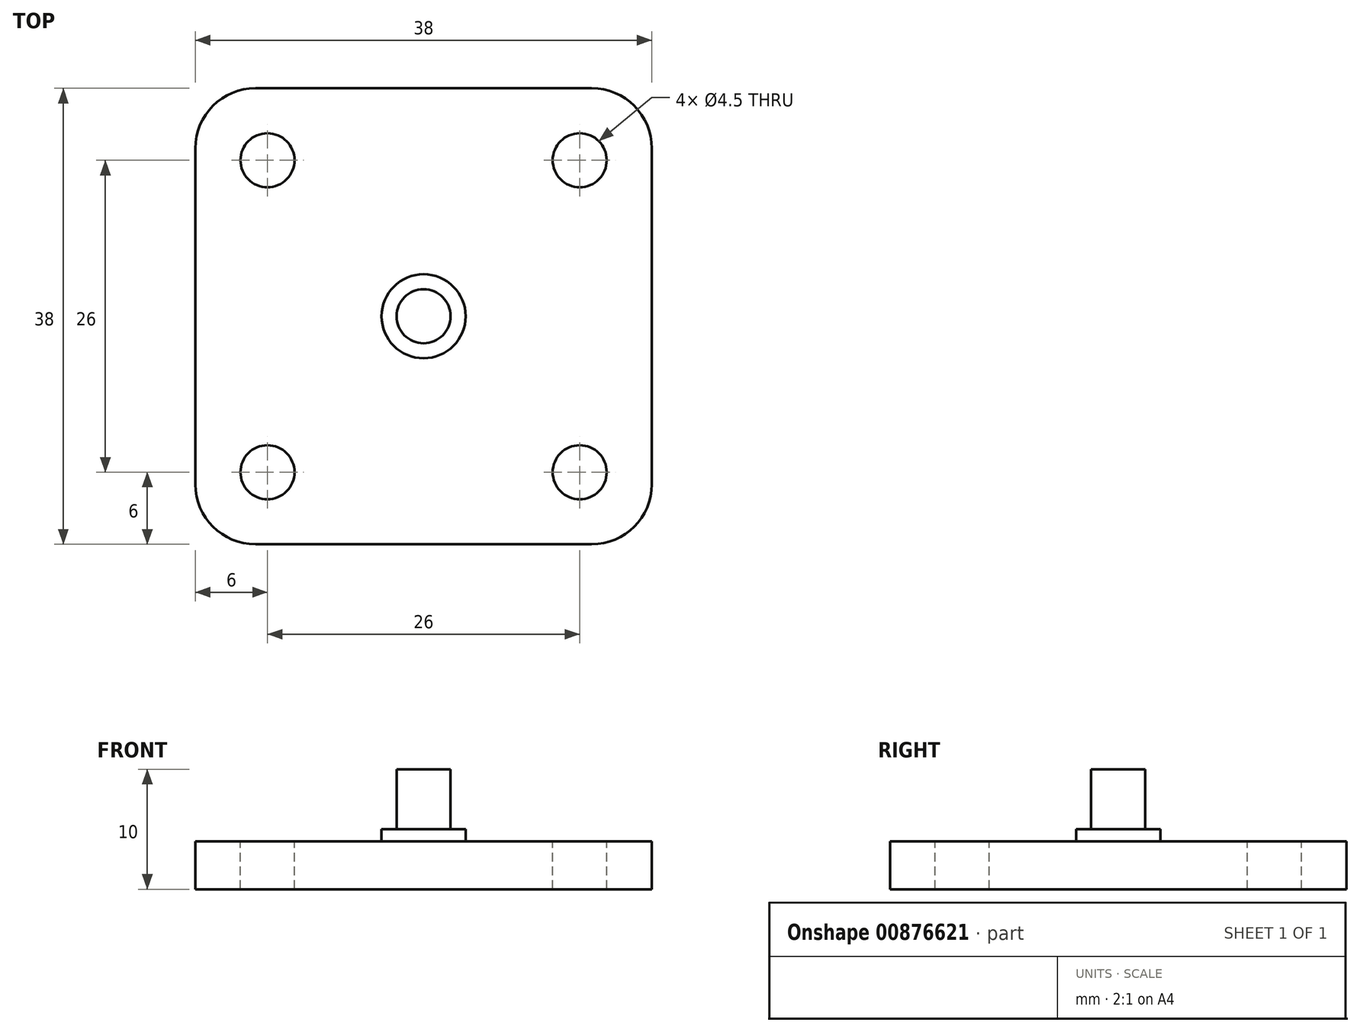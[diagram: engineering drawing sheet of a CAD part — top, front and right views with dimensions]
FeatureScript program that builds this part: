
annotation { "Feature Type Name" : "Feature", "Feature Type Description" : "" }
export const myFeature = defineFeature(function(context is Context, id is Id, definition is map)
    precondition{}
    {
        {
            var Q0;
            Q0=qCreatedBy(makeId("Top.planeOp"),FACE);
            var sketch = newSketch(context, id + "F0", { "sketchPlane" : qUnion([Q0])});
            skLineSegment(sketch, "E0.bottom", {"start": v(19, 19) * mm, "end": v(-19, 19) * mm});
            skLineSegment(sketch, "E0.top", {"start": v(19, -19) * mm, "end": v(-19, -19) * mm});
            skLineSegment(sketch, "E0.left", {"start": v(19, 19) * mm, "end": v(19, -19) * mm});
            skLineSegment(sketch, "E0.right", {"start": v(-19, 19) * mm, "end": v(-19, -19) * mm});
            skPoint(sketch, "E0.middle", {"position": v(0, 0) * mm});
            skLineSegment(sketch, "E1.0", {"start": v(19, 13) * mm, "end": v(-19, 13) * mm, "construction": true});
            skLineSegment(sketch, "E2.0", {"start": v(-13, 19) * mm, "end": v(-13, -19) * mm, "construction": true});
            skLineSegment(sketch, "E3.0", {"start": v(13, 19) * mm, "end": v(13, -19) * mm, "construction": true});
            skLineSegment(sketch, "E4.0", {"start": v(19, -13) * mm, "end": v(-19, -13) * mm, "construction": true});
            skCircle(sketch, "E5", {"center": v(-13, 13) * mm, "radius": 2.25 * mm});
            skLineSegment(sketch, "E6", {"start": v(-19, 0) * mm, "end": v(19, 0) * mm, "construction": true});
            skLineSegment(sketch, "E7", {"start": v(0, 19) * mm, "end": v(0, -19) * mm, "construction": true});
            skCircle(sketch, "E8.MirrorC", {"center": v(13, 13) * mm, "radius": 2.25 * mm});
            skCircle(sketch, "E9.MirrorC", {"center": v(13, -13) * mm, "radius": 2.25 * mm});
            skCircle(sketch, "E10.MirrorC", {"center": v(-13, -13) * mm, "radius": 2.25 * mm});
            skCircle(sketch, "E11", {"center": v(0, 0) * mm, "radius": 3.5 * mm});
            skCircle(sketch, "E12", {"center": v(0, 0) * mm, "radius": 2.25 * mm});
            skSolve(sketch);
        }
        {
            var Q0;
            Q0=makeQuery(id+"F0.imprint","IMPRINT",FACE,{"disambiguationData":[TD([[makeQuery(id+"F0.imprint","IMPRINT",EDGE,{"derivedFrom":sQuery(id+"F0.wireOp",EDGE,"E0.bottom")}),1.0]])]});
            var Q1;
            Q1=makeQuery(id+"F0.imprint","IMPRINT",FACE,{"disambiguationData":[TD([[makeQuery(id+"F0.imprint","IMPRINT",EDGE,{"derivedFrom":sQuery(id+"F0.wireOp",EDGE,"E11")}),1.0]])]});
            var Q2;
            Q2=makeQuery(id+"F0.imprint","IMPRINT",FACE,{"disambiguationData":[TD([[makeQuery(id+"F0.imprint","IMPRINT",EDGE,{"derivedFrom":sQuery(id+"F0.wireOp",EDGE,"E12")}),1.0]])]});
            extrude(context, id + "F1", {"entities" : qUnion([Q0, Q1, Q2]), "oppositeDirection" : true, "depth" : 4 * mm, "offsetDistance" : 25 * mm});
        }
        {
            var Q0;
            Q0=makeQuery(id+"F0.imprint","IMPRINT",FACE,{"disambiguationData":[TD([[makeQuery(id+"F0.imprint","IMPRINT",EDGE,{"derivedFrom":sQuery(id+"F0.wireOp",EDGE,"E11")}),1.0]])]});
            extrude(context, id + "F2", {"entities" : qUnion([Q0]), "operationType" : NewBodyOperationType.ADD, "depth" : 1 * mm, "offsetDistance" : 25 * mm});
        }
        {
            var Q0;
            Q0=makeQuery(id+"F0.imprint","IMPRINT",FACE,{"disambiguationData":[TD([[makeQuery(id+"F0.imprint","IMPRINT",EDGE,{"derivedFrom":sQuery(id+"F0.wireOp",EDGE,"E12")}),1.0]])]});
            extrude(context, id + "F3", {"entities" : qUnion([Q0]), "operationType" : NewBodyOperationType.ADD, "depth" : 6 * mm, "offsetDistance" : 25 * mm});
        }
        {
            var Q0;
            Q0=makeQuery(id+"F1.opExtrude","SWEPT_EDGE",EDGE,{"disambiguationData":[OSD([sQuery(id+"F0.wireOp",EDGE,"E0.top"),sQuery(id+"F0.wireOp",EDGE,"E0.right")])]});
            var Q1;
            Q1=makeQuery(id+"F1.opExtrude","SWEPT_EDGE",EDGE,{"disambiguationData":[OSD([sQuery(id+"F0.wireOp",EDGE,"E0.top"),sQuery(id+"F0.wireOp",EDGE,"E0.left")])]});
            var Q2;
            Q2=makeQuery(id+"F1.opExtrude","SWEPT_EDGE",EDGE,{"disambiguationData":[OSD([sQuery(id+"F0.wireOp",EDGE,"E0.bottom"),sQuery(id+"F0.wireOp",EDGE,"E0.left")])]});
            var Q3;
            Q3=makeQuery(id+"F1.opExtrude","SWEPT_EDGE",EDGE,{"disambiguationData":[OSD([sQuery(id+"F0.wireOp",EDGE,"E0.bottom"),sQuery(id+"F0.wireOp",EDGE,"E0.right")])]});
            fillet(context, id + "F4", {"entities" : qUnion([Q0, Q1, Q2, Q3]), "radius" : 5 * mm, "tangentPropagation" : true, "allowEdgeOverflow" : false});
        }
    });
